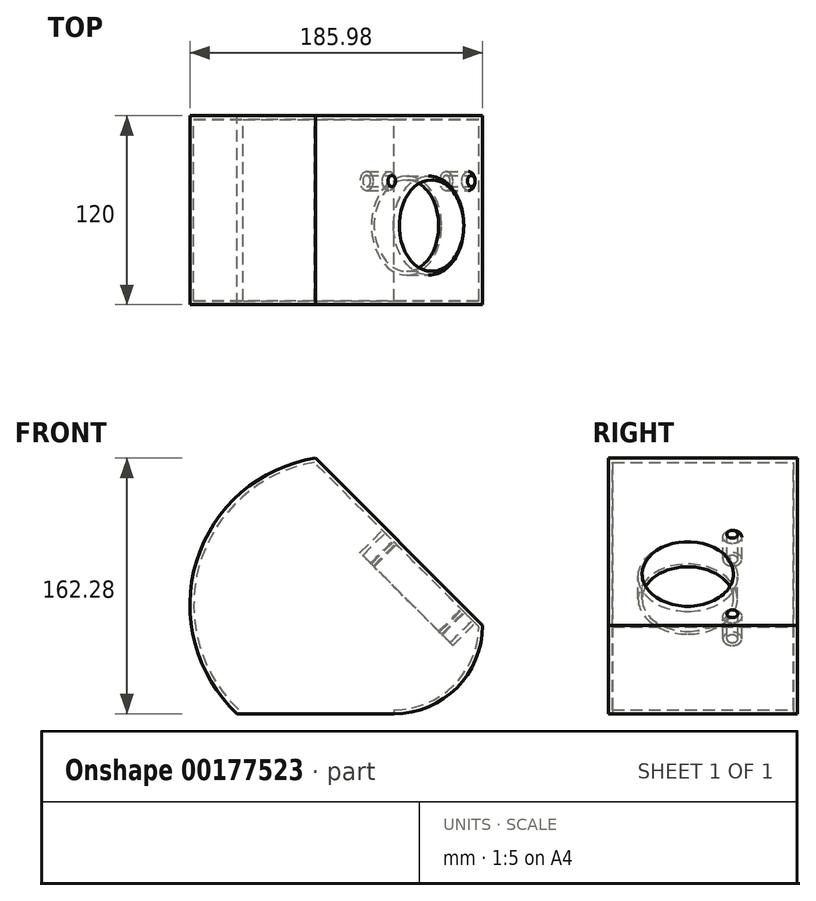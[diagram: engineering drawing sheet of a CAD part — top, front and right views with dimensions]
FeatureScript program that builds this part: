
annotation { "Feature Type Name" : "Feature", "Feature Type Description" : "" }
export const myFeature = defineFeature(function(context is Context, id is Id, definition is map)
    precondition{}
    {
        {
            var Q0;
            Q0=qCreatedBy(makeId("Front.planeOp"),FACE);
            var sketch = newSketch(context, id + "F0", { "sketchPlane" : qUnion([Q0])});
            skLineSegment(sketch, "E0", {"start": v(121.24, 56.22) * mm, "end": v(15.18, 162.28) * mm});
            skLineSegment(sketch, "E1", {"start": v(-34.67, 0) * mm, "end": v(65.03, 0) * mm});
            skArc(sketch, "E2", {"start": v(15.18, 162.28) * mm, "mid": v(-60.58, 96.76) * mm, "end": v(-34.67, 0) * mm});
            skArc(sketch, "E3", {"start": v(65.03, 0) * mm, "mid": v(104.78, 16.47) * mm, "end": v(121.24, 56.22) * mm});
            skSolve(sketch);
        }
        {
            var Q0;
            Q0=makeQuery(id+"F0.imprint","IMPRINT",FACE,{"disambiguationData":[TD([[makeQuery(id+"F0.imprint","IMPRINT",EDGE,{"derivedFrom":sQuery(id+"F0.wireOp",EDGE,"E0")}),1.0]])]});
            extrude(context, id + "F1", {"entities" : qUnion([Q0]), "depth" : 120 * mm, "symmetric" : true});
        }
        {
            var Q0;
            Q0=makeQuery(id+"F1.opExtrude","SWEPT_FACE",FACE,{"disambiguationData":[OSD([sQuery(id+"F0.wireOp",EDGE,"E0")])]});
            var sketch = newSketch(context, id + "F2", { "sketchPlane" : qUnion([Q0])});
            skLineSegment(sketch, "E4.bottom", {"start": v(24.06, 43.2) * mm, "end": v(-80.44, 43.2) * mm});
            skLineSegment(sketch, "E4.top", {"start": v(24.06, -43.2) * mm, "end": v(-80.44, -43.2) * mm});
            skLineSegment(sketch, "E4.left", {"start": v(26.06, 41.2) * mm, "end": v(26.06, -41.2) * mm});
            skLineSegment(sketch, "E4.right", {"start": v(-82.44, 41.2) * mm, "end": v(-82.44, -41.2) * mm});
            skPoint(sketch, "E4.middle", {"position": v(-28.19, 0) * mm});
            skPoint(sketch, "E5.visualSharp", {"position": v(-82.44, -43.2) * mm});
            skArc(sketch, "E5.filletArc", {"start": v(-82.44, -41.2) * mm, "mid": v(-81.85, -42.61) * mm, "end": v(-80.44, -43.2) * mm});
            skPoint(sketch, "E6.visualSharp", {"position": v(-82.44, 43.2) * mm});
            skArc(sketch, "E6.filletArc", {"start": v(-80.44, 43.2) * mm, "mid": v(-81.85, 42.61) * mm, "end": v(-82.44, 41.2) * mm});
            skPoint(sketch, "E7.visualSharp", {"position": v(26.06, 43.2) * mm});
            skArc(sketch, "E7.filletArc", {"start": v(26.06, 41.2) * mm, "mid": v(25.48, 42.61) * mm, "end": v(24.06, 43.2) * mm});
            skPoint(sketch, "E8.visualSharp", {"position": v(26.06, -43.2) * mm});
            skArc(sketch, "E8.filletArc", {"start": v(24.06, -43.2) * mm, "mid": v(25.48, -42.61) * mm, "end": v(26.06, -41.2) * mm});
            skCircle(sketch, "E9", {"center": v(-9.74, 0) * mm, "radius": 29 * mm});
            skCircle(sketch, "E10", {"center": v(-74.94, -35.7) * mm, "radius": 3.5 * mm});
            skCircle(sketch, "E11", {"center": v(-74.94, 35.7) * mm, "radius": 3.5 * mm});
            skCircle(sketch, "E12", {"center": v(18.56, 35.7) * mm, "radius": 3.5 * mm});
            skCircle(sketch, "E13", {"center": v(18.56, -35.7) * mm, "radius": 3.5 * mm});
            skSolve(sketch);
        }
        {
            var Q0;
            Q0=makeQuery(id+"F2.imprint","IMPRINT",FACE,{"disambiguationData":[TD([[makeQuery(id+"F2.imprint","IMPRINT",EDGE,{"derivedFrom":sQuery(id+"F2.wireOp",EDGE,"E4.bottom")}),1.0]])]});
            var Q1;
            Q1=makeQuery(id+"F2.imprint","IMPRINT",FACE,{"disambiguationData":[TD([[makeQuery(id+"F2.imprint","IMPRINT",EDGE,{"derivedFrom":sQuery(id+"F2.wireOp",EDGE,"E9")}),1.0]])]});
            var Q2;
            Q2=makeQuery(id+"F2.imprint","IMPRINT",FACE,{"disambiguationData":[TD([[makeQuery(id+"F2.imprint","IMPRINT",EDGE,{"derivedFrom":sQuery(id+"F2.wireOp",EDGE,"E10")}),1.0]])]});
            var Q3;
            Q3=makeQuery(id+"F2.imprint","IMPRINT",FACE,{"disambiguationData":[TD([[makeQuery(id+"F2.imprint","IMPRINT",EDGE,{"derivedFrom":sQuery(id+"F2.wireOp",EDGE,"E11")}),1.0]])]});
            var Q4;
            Q4=makeQuery(id+"F2.imprint","IMPRINT",FACE,{"disambiguationData":[TD([[makeQuery(id+"F2.imprint","IMPRINT",EDGE,{"derivedFrom":sQuery(id+"F2.wireOp",EDGE,"E12")}),1.0]])]});
            var Q5;
            Q5=makeQuery(id+"F2.imprint","IMPRINT",FACE,{"disambiguationData":[TD([[makeQuery(id+"F2.imprint","IMPRINT",EDGE,{"derivedFrom":sQuery(id+"F2.wireOp",EDGE,"E13")}),1.0]])]});
            extrude(context, id + "F3", {"entities" : qUnion([Q0, Q1, Q2, Q3, Q4, Q5]), "operationType" : NewBodyOperationType.REMOVE, "oppositeDirection" : true, "depth" : 20 * mm});
        }
        {
            var Q0;
            Q0=makeQuery(id+"F1.opExtrude","SWEPT_FACE",FACE,{"disambiguationData":[OSD([sQuery(id+"F0.wireOp",EDGE,"E1")])]});
            shell(context, id + "F4", {"entities" : qUnion([Q0]), "thickness" : 2.5 * mm});
        }
        {
            var Q0;
            Q0=makeQuery(id+"F2.imprint","IMPRINT",FACE,{"disambiguationData":[TD([[makeQuery(id+"F2.imprint","IMPRINT",EDGE,{"derivedFrom":sQuery(id+"F2.wireOp",EDGE,"E9")}),1.0]])]});
            var Q1;
            Q1=makeQuery(id+"F2.imprint","IMPRINT",FACE,{"disambiguationData":[TD([[makeQuery(id+"F2.imprint","IMPRINT",EDGE,{"derivedFrom":sQuery(id+"F2.wireOp",EDGE,"E11")}),1.0]])]});
            var Q2;
            Q2=makeQuery(id+"F2.imprint","IMPRINT",FACE,{"disambiguationData":[TD([[makeQuery(id+"F2.imprint","IMPRINT",EDGE,{"derivedFrom":sQuery(id+"F2.wireOp",EDGE,"E10")}),1.0]])]});
            var Q3;
            Q3=makeQuery(id+"F2.imprint","IMPRINT",FACE,{"disambiguationData":[TD([[makeQuery(id+"F2.imprint","IMPRINT",EDGE,{"derivedFrom":sQuery(id+"F2.wireOp",EDGE,"E13")}),1.0]])]});
            var Q4;
            Q4=makeQuery(id+"F2.imprint","IMPRINT",FACE,{"disambiguationData":[TD([[makeQuery(id+"F2.imprint","IMPRINT",EDGE,{"derivedFrom":sQuery(id+"F2.wireOp",EDGE,"E12")}),1.0]])]});
            extrude(context, id + "F5", {"entities" : qUnion([Q0, Q1, Q2, Q3, Q4]), "operationType" : NewBodyOperationType.REMOVE, "oppositeDirection" : true, "depth" : 40 * mm});
        }
    });
